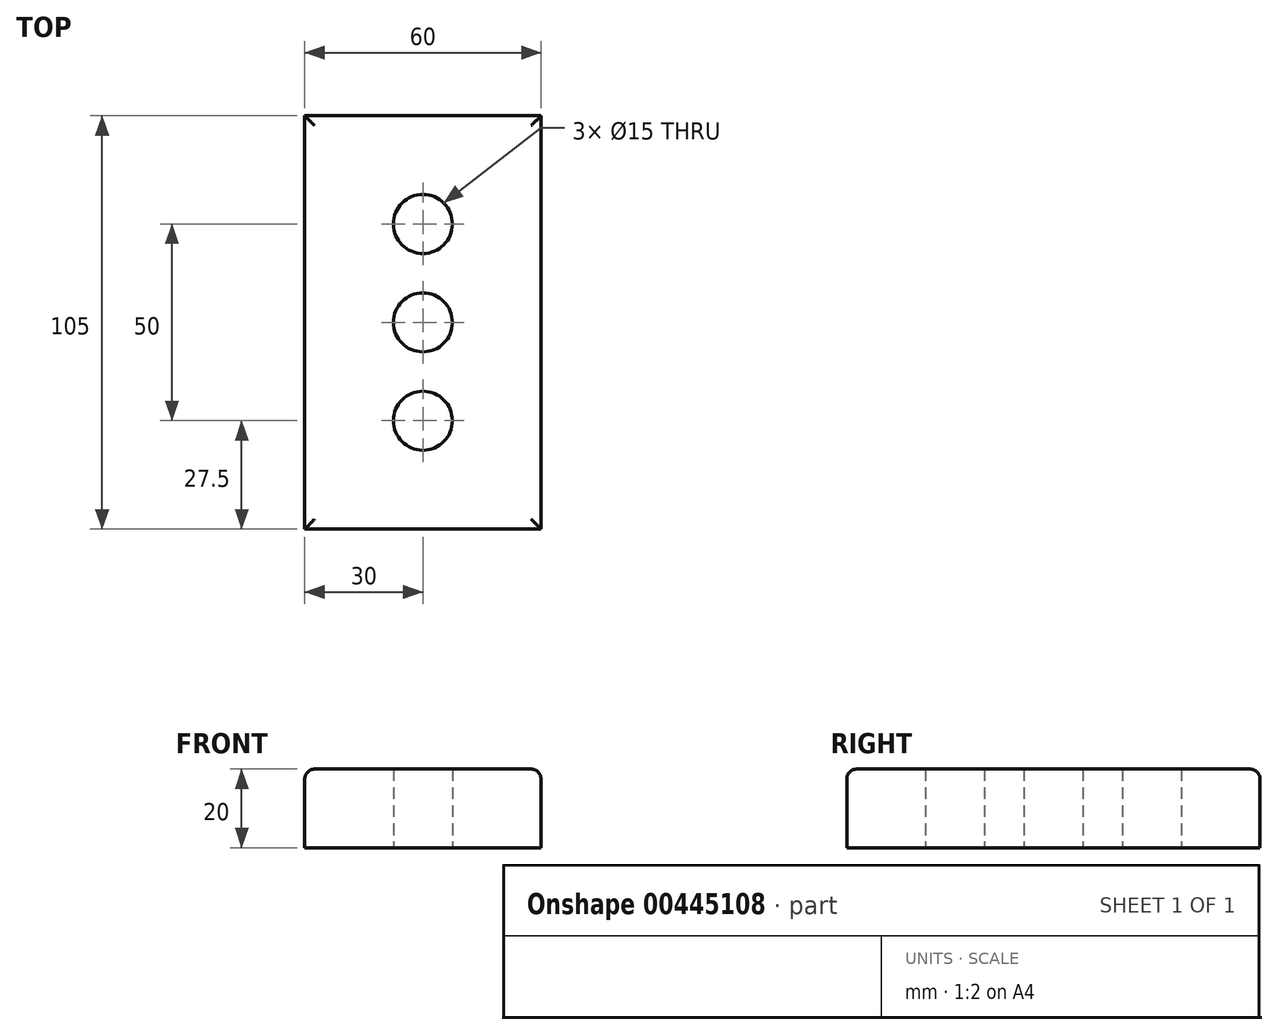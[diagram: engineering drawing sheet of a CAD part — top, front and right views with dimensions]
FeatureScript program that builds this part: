
annotation { "Feature Type Name" : "Feature", "Feature Type Description" : "" }
export const myFeature = defineFeature(function(context is Context, id is Id, definition is map)
    precondition{}
    {
        {
            var Q0;
            Q0=qCreatedBy(makeId("Top.planeOp"),FACE);
            var sketch = newSketch(context, id + "F0", { "sketchPlane" : qUnion([Q0])});
            skLineSegment(sketch, "E0.bottom", {"start": v(-30, 52.5) * mm, "end": v(30, 52.5) * mm});
            skLineSegment(sketch, "E0.top", {"start": v(-30, -52.5) * mm, "end": v(30, -52.5) * mm});
            skLineSegment(sketch, "E0.left", {"start": v(-30, 52.5) * mm, "end": v(-30, -52.5) * mm});
            skLineSegment(sketch, "E0.right", {"start": v(30, 52.5) * mm, "end": v(30, -52.5) * mm});
            skPoint(sketch, "E0.middle", {"position": v(0, 0) * mm});
            skCircle(sketch, "E1", {"center": v(0, 0) * mm, "radius": 7.5 * mm});
            skLineSegment(sketch, "E2", {"start": v(0, 7.5) * mm, "end": v(0, 25) * mm});
            skLineSegment(sketch, "E3", {"start": v(0, -7.5) * mm, "end": v(0, -25) * mm});
            skCircle(sketch, "E4", {"center": v(0, 25) * mm, "radius": 7.5 * mm});
            skCircle(sketch, "E5", {"center": v(0, -25) * mm, "radius": 7.5 * mm});
            skSolve(sketch);
        }
        {
            var Q0;
            Q0 = qSketchRegion(id + "F0", true);
            extrude(context, id + "F1", {"entities" : qUnion([Q0]), "depth" : 20 * mm});
        }
        {
            var Q0;
            Q0=makeQuery(id+"F1.opExtrude","CAP_EDGE",EDGE,{"disambiguationData":[OSD([sQuery(id+"F0.wireOp",EDGE,"E0.top")])],"isStart":false});
            var Q1;
            Q1=makeQuery(id+"F1.opExtrude","CAP_EDGE",EDGE,{"disambiguationData":[OSD([sQuery(id+"F0.wireOp",EDGE,"E0.right")])],"isStart":false});
            var Q2;
            Q2=makeQuery(id+"F1.opExtrude","CAP_EDGE",EDGE,{"disambiguationData":[OSD([sQuery(id+"F0.wireOp",EDGE,"E0.left")])],"isStart":false});
            var Q3;
            Q3=makeQuery(id+"F1.opExtrude","CAP_EDGE",EDGE,{"disambiguationData":[OSD([sQuery(id+"F0.wireOp",EDGE,"E0.bottom")])],"isStart":false});
            fillet(context, id + "F2", {"entities" : qUnion([Q0, Q1, Q2, Q3]), "radius" : 2.5 * mm, "tangentPropagation" : true, "allowEdgeOverflow" : false});
        }
    });
